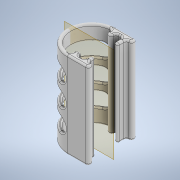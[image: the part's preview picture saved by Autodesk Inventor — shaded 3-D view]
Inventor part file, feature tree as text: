
AUTODESK INVENTOR PART (.ipt)
format: ipt  version: 2020 (Build 240168000, 168)  size: 560,128 bytes
history: native  units: in
note: dims shown in document units (in); Inventor stores cm internally (conversion verified against a paired STEP export)
features: fillet x5, extrude x2, sketch x2, plane x1
ambient origin geometry x8: Origin, YZ Plane, XZ Plane, XY Plane, X Axis, Y Axis, Z Axis, Center Point
bodies: Solid1 (feature_tree)
feature tree (10):
  extrude  "Extrusion1"  Depth=0.1181in
  fillet  "Fillet1"  Radius=0.7874in
  fillet  "Fillet2"  Radius=0.0787in
  fillet  "Fillet3"  Radius=0.1575in
  fillet  "Fillet4"  Radius=0.0787in
  plane  "Work Plane1"
  extrude  "Extrusion2"  Depth=0.0787in
  fillet  "Fillet5"  Radius=0.0394in
  sketch  "Sketch1"  dims[d0=0.0787in d1=0.1181in d2=0.7874in d3=0.0787in d4=0.1575in d5=0.0787in]
  sketch  "Sketch2"  dims[d6=0.0394in d7=0.0787in d8=0.0394in d9=0.2362in d10=0.1181in d11=0.2362in d12=0.1181in d13=0.1181in d14=0.1181in d15=0.217in d16=0.1181in d17=0.1181in d18=0.1181in d19=0.1181in d20=0.5512in d21=0.0787in d22=0.0787in d23=1.9685in d24=0.0in d25=0.0591in d26=0.0394in d27=0.0591in d28=0.0394in d29=-0.375in d30=1.9685in d31=0.4921in d32=0.4921in d33=0.4921in d34=0.315in d35=0.315in d36=0.315in d37=1.9685in d38=0.0in d39=0.0315in]
